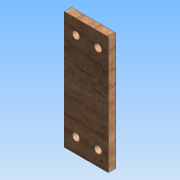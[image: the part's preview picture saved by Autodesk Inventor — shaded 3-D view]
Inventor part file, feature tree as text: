
AUTODESK INVENTOR PART (.ipt)
format: ipt  version: 2015 (Build 190159000, 159)  size: 164,352 bytes
history: native  units: mm
features: other x5, extrude x1, sketch x1
ambient origin geometry x8: Origin, YZ Plane, XZ Plane, XY Plane, X Axis, Y Axis, Z Axis, Center Point
bodies: Body1 (feature_tree)
feature tree (7):
  other  "Blocks"
  extrude  "Extrusion12"  Depth=5.0mm
  other  "Block1"
  other  "Block2"
  other  "Block3"
  other  "Block4"
  sketch  "Sketch45"  dims[d197=5.0mm d199=5.0mm d200=5.0mm d201=60.0mm d202=80.0mm d203=10.0mm d204=10.0mm d205=15.0mm d206=30.0mm d207=8.0mm d210=5.0mm d211=5.0mm d212=0.0mm d29=1.0mm d30=1.0mm]
